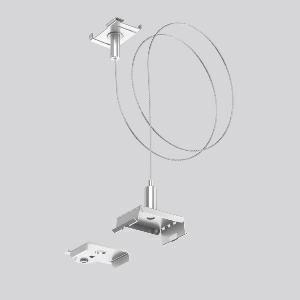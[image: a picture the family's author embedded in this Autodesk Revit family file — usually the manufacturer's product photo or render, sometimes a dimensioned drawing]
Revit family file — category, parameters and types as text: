
# Revit family: linedo_pendelset_5m_seil_caddyclip_982719_000_baf2
name_source: partatom
category: Lighting Fixtures
units: mm (PartAtom-declared; Revit-internal decimal feet)

## family parameters
Cut with Voids When Loaded = No
Host = Face
Light Source = No
Part Type = Normal
Room Calculation Point = No
Round Connector Dimension = Use Diameter
Shared = No

## types (1)
- LINEDO Pendelset 5m Seil Caddyclip
    Apparent Load = 0 VA
    Default Elevation = 1800 mm
    Description = Suspension kit for grid ceilings with steel cable 5,000 mm and caddy clip. Spring steel, blank, for installing continuous line luminaire modules.
Colour: stainless steel
Length: 54 mm
Width: 30 mm
Height: 42 mm
Weight: 265 g
Type of Installation: pendant
    Height = 43 mm
    Lamp = 0 x
    Length = 54 mm
    Luminous efficacy = 0 lm/W
    Manufacturer = RZB
    ModVariant = No
    Model = 982719.000
    Mounting Place = Ceiling
    Mounting Type = Surface mounted
    Number of Poles = 1
    OnlyDefault = Yes
    Power Factor = 1
    Product Name = LINEDO Pendelset 5m Seil Caddyclip
    Product group = Surface mounted continuous line luminaire system
    ProductGroupID = 310
    Protection Class = Protection class
    Protection Degree = Degree of protection
    RLX_Detail_Level = 1
    RLX_Emergency_Light_Flux = 0 lm
    RLX_Emergency_Type = 0
    RLX_Emergency_Type_DB = No
    RlxData = <blob elided: 23957 chars, md5=e0a3cb98>
    Standby Power = 0 W
    System Light Flux = 0 lm
    System Power = 0 W
    Type Comments = Product without accessories
    Type Image = 982719.000.jpg
    URL = http://relux.com
    VarID = ---
    Voltage = 0 V
    Weight = 0.00 kg
    Width = 30 mm  [stored 0.0984252 ft]

note: [stored X ft] marks values corroborated as IEEE doubles in the binary element streams (Revit-internal decimal feet)

## geometry (parser evidence)
native form markers: Blend x4, Sweep x10
no freeform markers — native parametric forms only
